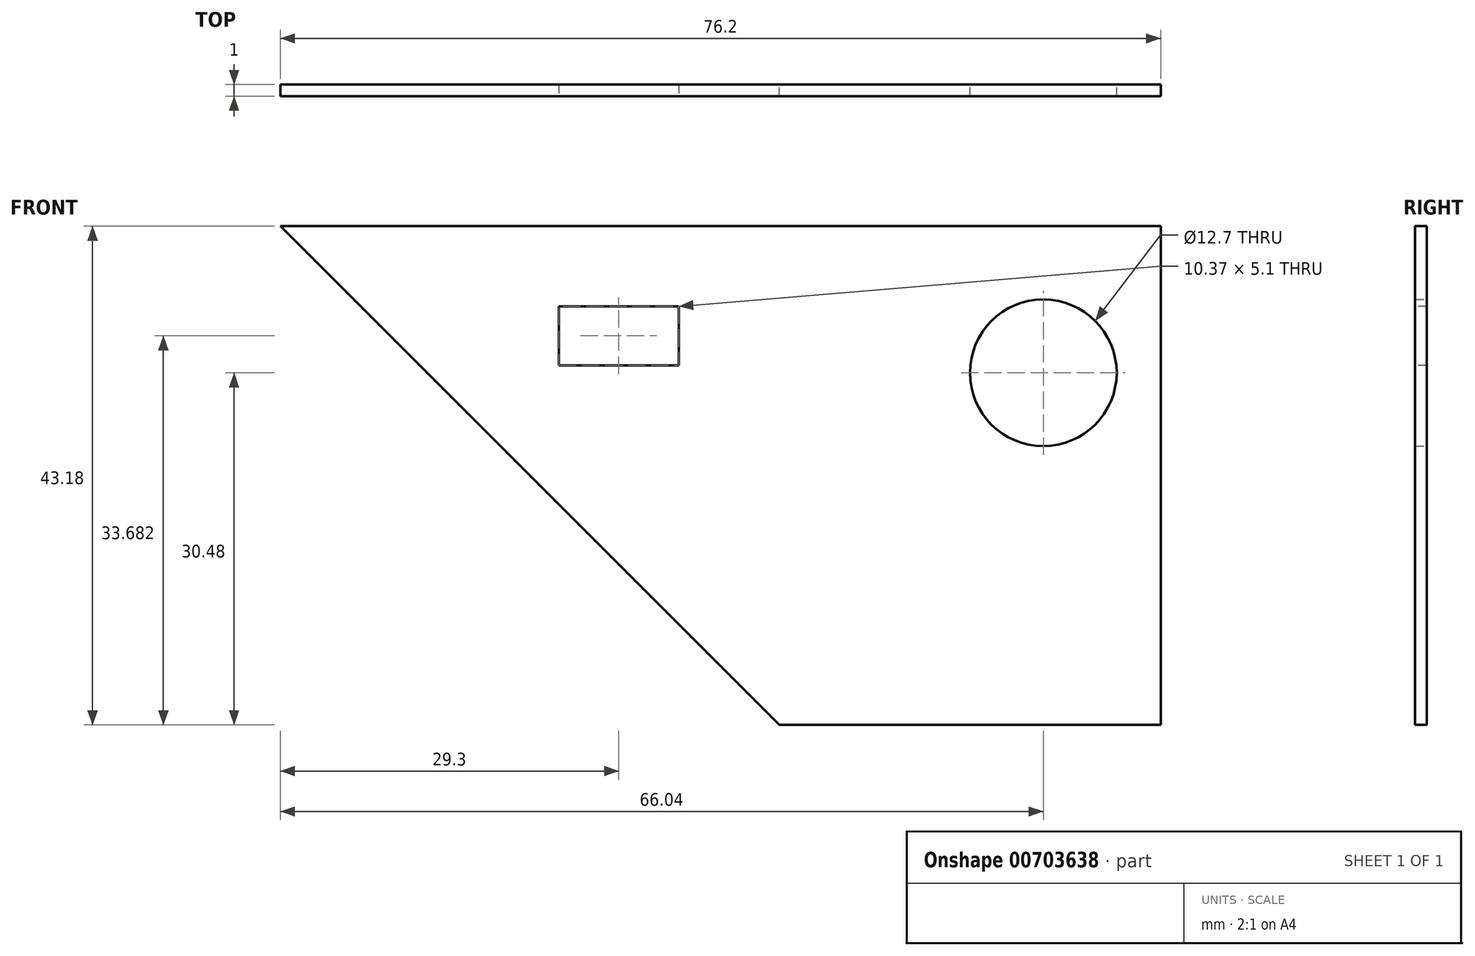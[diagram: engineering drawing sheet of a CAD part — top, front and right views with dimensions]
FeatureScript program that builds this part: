
annotation { "Feature Type Name" : "Feature", "Feature Type Description" : "" }
export const myFeature = defineFeature(function(context is Context, id is Id, definition is map)
    precondition{}
    {
        {
            var Q0;
            Q0=qCreatedBy(makeId("Front.planeOp"),FACE);
            var sketch = newSketch(context, id + "F0", { "sketchPlane" : qUnion([Q0])});
            skLineSegment(sketch, "E0", {"start": v(0, 0) * mm, "end": v(-43.18, 43.18) * mm});
            skLineSegment(sketch, "E1", {"start": v(-43.18, 43.18) * mm, "end": v(33.02, 43.18) * mm});
            skLineSegment(sketch, "E2", {"start": v(33.02, 43.18) * mm, "end": v(33.02, 0) * mm});
            skLineSegment(sketch, "E3", {"start": v(33.02, 0) * mm, "end": v(0, 0) * mm});
            skSolve(sketch);
        }
        {
            var Q0;
            Q0=makeQuery(id+"F0.imprint","IMPRINT",FACE,{"disambiguationData":[TD([[makeQuery(id+"F0.imprint","IMPRINT",EDGE,{"derivedFrom":sQuery(id+"F0.wireOp",EDGE,"E0")}),-1.0]])]});
            var Q1;
            Q1=sQuery(id+"F0.wireOp",EDGE,"E1");
            var Q2;
            Q2=sQuery(id+"F0.wireOp",EDGE,"E2");
            var Q3;
            Q3=sQuery(id+"F0.wireOp",EDGE,"E3");
            var Q4;
            Q4=sQuery(id+"F0.wireOp",EDGE,"E0");
            extrude(context, id + "F1", {"entities" : qUnion([Q0]), "surfaceEntities" : qUnion([Q1, Q2, Q3, Q4]), "endBound" : BoundingType.SYMMETRIC, "depth" : 1 * mm, "offsetDistance" : 25.4 * mm});
        }
        {
            var Q0;
            Q0=qCreatedBy(makeId("Front.planeOp"),FACE);
            var sketch = newSketch(context, id + "F2", { "sketchPlane" : qUnion([Q0])});
            skCircle(sketch, "E4", {"center": v(22.86, 30.48) * mm, "radius": 6.35 * mm});
            skSolve(sketch);
        }
        {
            var Q0;
            Q0=qSketchRegion(id+"F2",true);
            extrude(context, id + "F3", {"entities" : qUnion([Q0]), "operationType" : NewBodyOperationType.REMOVE, "endBound" : BoundingType.SYMMETRIC, "depth" : 25.4 * mm, "offsetDistance" : 25.4 * mm});
        }
        {
            var Q0;
            Q0=qCreatedBy(makeId("Front.planeOp"),FACE);
            var sketch = newSketch(context, id + "F4", { "sketchPlane" : qUnion([Q0])});
            skLineSegment(sketch, "E5.bottom", {"start": v(-19.07, 36.23) * mm, "end": v(-8.7, 36.23) * mm});
            skLineSegment(sketch, "E5.top", {"start": v(-19.07, 31.13) * mm, "end": v(-8.7, 31.13) * mm});
            skLineSegment(sketch, "E5.left", {"start": v(-19.07, 36.23) * mm, "end": v(-19.07, 31.13) * mm});
            skLineSegment(sketch, "E5.right", {"start": v(-8.7, 36.23) * mm, "end": v(-8.7, 31.13) * mm});
            skSolve(sketch);
        }
        {
            var Q0;
            Q0 = qSketchRegion(id + "F4", true);
            extrude(context, id + "F5", {"entities" : qUnion([Q0]), "operationType" : NewBodyOperationType.REMOVE, "endBound" : BoundingType.SYMMETRIC, "oppositeDirection" : true, "depth" : 25.4 * mm, "offsetDistance" : 25.4 * mm});
        }
    });
